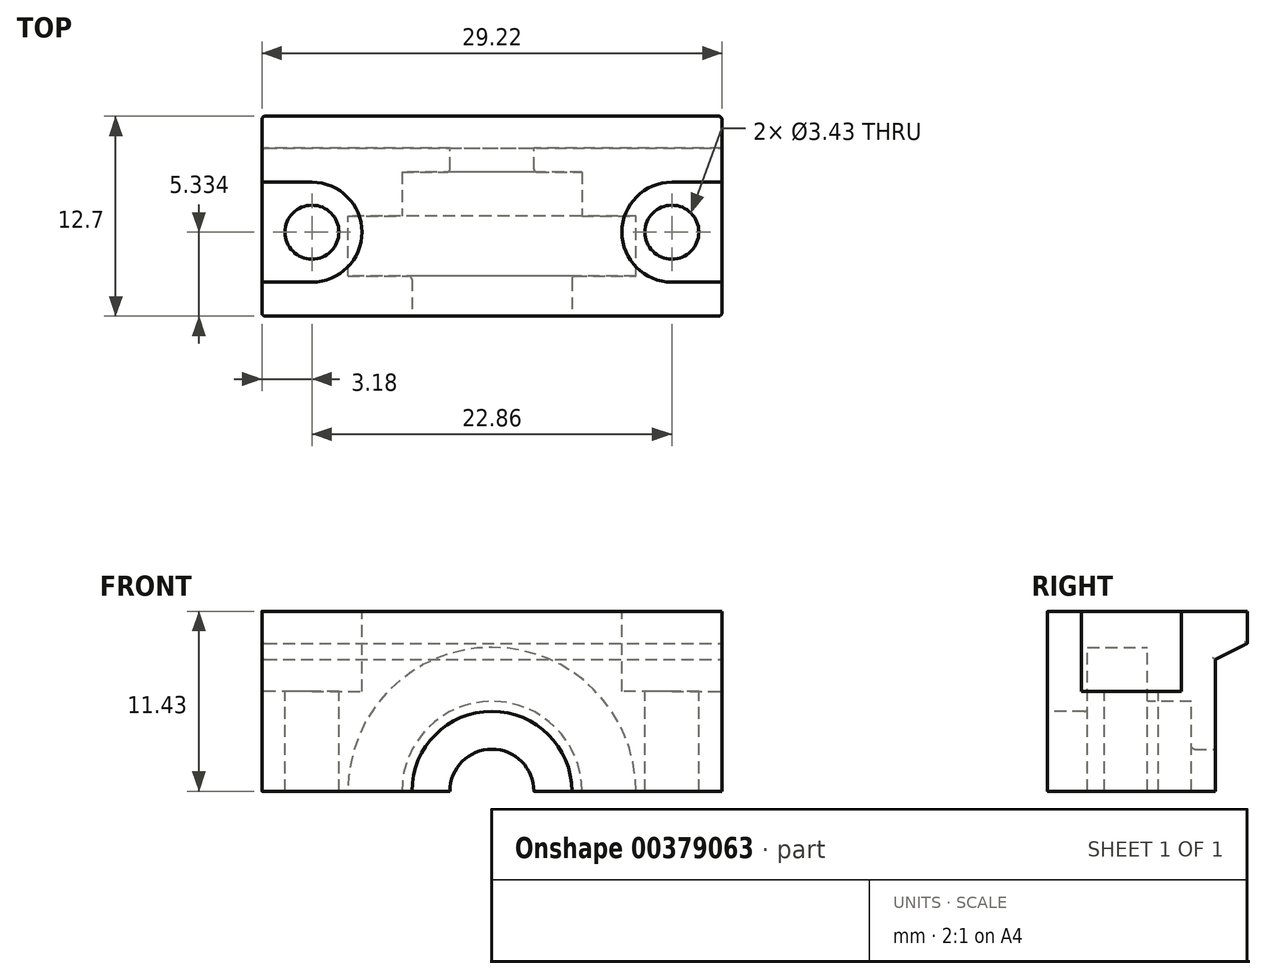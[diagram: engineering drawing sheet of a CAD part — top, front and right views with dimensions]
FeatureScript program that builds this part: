
annotation { "Feature Type Name" : "Feature", "Feature Type Description" : "" }
export const myFeature = defineFeature(function(context is Context, id is Id, definition is map)
    precondition{}
    {
        {
            var Q0;
            Q0=qCreatedBy(makeId("Front.planeOp"),FACE);
            var sketch = newSketch(context, id + "F0", { "sketchPlane" : qUnion([Q0])});
            skLineSegment(sketch, "E0.bottom", {"start": v(14.6, -3.75) * mm, "end": v(-14.6, -3.75) * mm});
            skLineSegment(sketch, "E0.left", {"start": v(14.6, -3.75) * mm, "end": v(14.6, 3.75) * mm});
            skLineSegment(sketch, "E0.right", {"start": v(-14.6, -3.75) * mm, "end": v(-14.6, 3.75) * mm});
            skPoint(sketch, "E0.middle", {"position": v(0, 0) * mm});
            skArc(sketch, "E1", {"start": v(14.6, 3.75) * mm, "mid": v(0, 18.35) * mm, "end": v(-14.6, 3.75) * mm, "construction": true});
            skPoint(sketch, "E2", {"position": v(0, 18.35) * mm});
            skLineSegment(sketch, "E3", {"start": v(-14.6, 3.75) * mm, "end": v(-14.6, 18.35) * mm});
            skLineSegment(sketch, "E4", {"start": v(-14.6, 18.35) * mm, "end": v(14.6, 18.35) * mm});
            skLineSegment(sketch, "E5", {"start": v(14.6, 18.35) * mm, "end": v(14.6, 3.75) * mm});
            skSolve(sketch);
        }
        {
            var Q0;
            Q0=qSketchRegion(id+"F0",true);
            extrude(context, id + "F1", {"entities" : qUnion([Q0]), "depth" : 12.7 * mm});
        }
        {
            var Q0;
            Q0=qCreatedBy(makeId("Front.planeOp"),FACE);
            cPlane(context, id + "F2", {"entities" : qUnion([Q0]), "cplaneType" : CPlaneType.OFFSET, "offset" : 6.35 * mm, "width" : 152.4 * mm, "height" : 152.4 * mm});
        }
        {
            var Q0;
            Q0=qCreatedBy(id+"F2.planeOp",FACE);
            var sketch = newSketch(context, id + "F3", { "sketchPlane" : qUnion([Q0])});
            skLineSegment(sketch, "E6.bottom", {"start": v(9.14, -3.75) * mm, "end": v(-9.14, -3.75) * mm});
            skLineSegment(sketch, "E6.left", {"start": v(9.14, -3.75) * mm, "end": v(9.14, 6.92) * mm});
            skLineSegment(sketch, "E6.right", {"start": v(-9.14, -3.75) * mm, "end": v(-9.14, 6.92) * mm});
            skLineSegment(sketch, "E7", {"start": v(0, -3.75) * mm, "end": v(0, 19.01) * mm, "construction": true});
            skArc(sketch, "E8", {"start": v(9.14, 6.92) * mm, "mid": v(0, 16.07) * mm, "end": v(-9.14, 6.92) * mm});
            skPoint(sketch, "E9", {"position": v(0, 16.07) * mm});
            skSolve(sketch);
        }
        {
            var Q0;
            Q0=qSketchRegion(id+"F3",true);
            extrude(context, id + "F4", {"entities" : qUnion([Q0]), "operationType" : NewBodyOperationType.REMOVE, "depth" : 3.8 * mm});
        }
        {
            var Q0;
            Q0=makeQuery(id+"F1.opExtrude","CAP_FACE",FACE,{"disambiguationData":[OSD([sQuery(id+"F0.wireOp",EDGE,"E0.bottom"),sQuery(id+"F0.wireOp",EDGE,"E0.left"),sQuery(id+"F0.wireOp",EDGE,"E0.right"),sQuery(id+"F0.wireOp",EDGE,"E1")])],"isStart":false});
            var sketch = newSketch(context, id + "F5", { "sketchPlane" : qUnion([Q0])});
            skArc(sketch, "E10", {"start": v(4.85, 5.4) * mm, "mid": v(0, 12) * mm, "end": v(-4.85, 5.4) * mm});
            skLineSegment(sketch, "E11", {"start": v(4.85, 5.4) * mm, "end": v(-4.85, 5.4) * mm, "construction": true});
            skLineSegment(sketch, "E12", {"start": v(4.85, 5.4) * mm, "end": v(6.35, -3.75) * mm});
            skLineSegment(sketch, "E13", {"start": v(6.35, -3.75) * mm, "end": v(-6.35, -3.75) * mm});
            skLineSegment(sketch, "E14", {"start": v(-6.35, -3.75) * mm, "end": v(-4.85, 5.4) * mm});
            skLineSegment(sketch, "E15", {"start": v(0, -3.75) * mm, "end": v(0, 6.92) * mm, "construction": true});
            skSolve(sketch);
        }
        {
            var Q0;
            Q0=qSketchRegion(id+"F5",true);
            extrude(context, id + "F6", {"entities" : qUnion([Q0]), "operationType" : NewBodyOperationType.REMOVE, "oppositeDirection" : true, "depth" : 8.64 * mm});
        }
        {
            var Q0;
            Q0=makeQuery(id+"F1.opExtrude","SWEPT_FACE",FACE,{"disambiguationData":[OSD([sQuery(id+"F0.wireOp",EDGE,"E0.left")])]});
            var sketch = newSketch(context, id + "F7", { "sketchPlane" : qUnion([Q0])});
            skLineSegment(sketch, "E16", {"start": v(0, -1.71) * mm, "end": v(-2.03, -0.7) * mm});
            skLineSegment(sketch, "E17", {"start": v(-2.03, -0.7) * mm, "end": v(-2.03, 15.3) * mm});
            skLineSegment(sketch, "E18", {"start": v(-2.03, 15.3) * mm, "end": v(0, 16.32) * mm});
            skLineSegment(sketch, "E19", {"start": v(0, 16.32) * mm, "end": v(0, -1.71) * mm});
            skLineSegment(sketch, "E20", {"start": v(-2.03, 7.3) * mm, "end": v(0, 7.3) * mm, "construction": true});
            skPoint(sketch, "E20.startSnap0", {"position": v(0, 7.3) * mm});
            skSolve(sketch);
        }
        {
            var Q0;
            Q0=qSketchRegion(id+"F7",true);
            extrude(context, id + "F8", {"entities" : qUnion([Q0]), "operationType" : NewBodyOperationType.REMOVE, "endBound" : BoundingType.THROUGH_ALL, "oppositeDirection" : true, "depth" : 25.4 * mm});
        }
        {
            var Q0;
            Q0=makeQuery(id+"F8.boolean.opBoolean","COPY",FACE,{"derivedFrom":makeQuery(id+"F8.opExtrude","SWEPT_FACE",FACE,{"disambiguationData":[OSD([sQuery(id+"F7.wireOp",EDGE,"E17")])]})});
            var sketch = newSketch(context, id + "F9", { "sketchPlane" : qUnion([Q0])});
            skCircle(sketch, "E21", {"center": v(0, 6.92) * mm, "radius": 2.67 * mm});
            skSolve(sketch);
        }
        {
            var Q0;
            Q0=qSketchRegion(id+"F9",true);
            var Q1;
            Q1=qCreatedBy(id+"F2.planeOp",FACE);
            extrude(context, id + "F10", {"entities" : qUnion([Q0]), "operationType" : NewBodyOperationType.REMOVE, "endBound" : BoundingType.UP_TO_SURFACE, "oppositeDirection" : true, "endBoundEntityFace" : qUnion([Q1]), "depth" : 25.4 * mm});
        }
        {
            var Q0;
            Q0=makeQuery(id+"F1.opExtrude","SWEPT_FACE",FACE,{"disambiguationData":[OSD([sQuery(id+"F0.wireOp",EDGE,"E4")])]});
            var sketch = newSketch(context, id + "F11", { "sketchPlane" : qUnion([Q0])});
            skLineSegment(sketch, "E22", {"start": v(14.6, -7.37) * mm, "end": v(-14.6, -7.37) * mm, "construction": true});
            skArc(sketch, "E23", {"start": v(11.43, -4.2) * mm, "mid": v(8.25, -7.37) * mm, "end": v(11.43, -10.54) * mm});
            skLineSegment(sketch, "E24", {"start": v(0, -12.7) * mm, "end": v(0, 0) * mm, "construction": true});
            skLineSegment(sketch, "E25", {"start": v(11.43, -4.2) * mm, "end": v(14.6, -4.2) * mm});
            skLineSegment(sketch, "E26", {"start": v(14.6, -4.2) * mm, "end": v(14.6, -10.54) * mm});
            skLineSegment(sketch, "E27", {"start": v(14.6, -10.54) * mm, "end": v(11.43, -10.54) * mm});
            skLineSegment(sketch, "E28", {"start": v(11.43, -4.2) * mm, "end": v(11.43, -10.54) * mm, "construction": true});
            skArc(sketch, "E29.MirrorCS", {"start": v(-11.43, -4.2) * mm, "mid": v(-8.26, -7.37) * mm, "end": v(-11.43, -10.54) * mm});
            skLineSegment(sketch, "E30.MirrorCS", {"start": v(-11.43, -4.2) * mm, "end": v(-14.6, -4.2) * mm});
            skLineSegment(sketch, "E31.MirrorCS", {"start": v(-14.6, -10.54) * mm, "end": v(-11.43, -10.54) * mm});
            skLineSegment(sketch, "E32.MirrorCS", {"start": v(-14.6, -4.2) * mm, "end": v(-14.6, -10.54) * mm});
            skSolve(sketch);
        }
        {
            var Q0;
            Q0 = qSketchRegion(id + "F11", true);
            extrude(context, id + "F12", {"entities" : qUnion([Q0]), "operationType" : NewBodyOperationType.REMOVE, "oppositeDirection" : true, "depth" : 5.08 * mm});
        }
        {
            var Q0;
            Q0=makeQuery(id+"F12.boolean.opBoolean","COPY",FACE,{"derivedFrom":makeQuery(id+"F12.opExtrude","CAP_FACE",FACE,{"disambiguationData":[OSD([sQuery(id+"F11.wireOp",EDGE,"E23")])],"isStart":false})});
            var sketch = newSketch(context, id + "F13", { "sketchPlane" : qUnion([Q0])});
            skCircle(sketch, "E33", {"center": v(11.43, -7.37) * mm, "radius": 1.71 * mm});
            skCircle(sketch, "E34", {"center": v(-11.43, -7.37) * mm, "radius": 1.71 * mm});
            skSolve(sketch);
        }
        {
            var Q0;
            Q0 = qSketchRegion(id + "F13", true);
            extrude(context, id + "F14", {"entities" : qUnion([Q0]), "operationType" : NewBodyOperationType.REMOVE, "oppositeDirection" : true, "depth" : 12.7 * mm});
        }
        {
            var Q0;
            Q0=makeQuery(id+"F4.boolean.opBoolean","COPY",FACE,{"derivedFrom":makeQuery(id+"F4.opExtrude","CAP_FACE",FACE,{"disambiguationData":[OSD([sQuery(id+"F3.wireOp",EDGE,"E6.bottom"),sQuery(id+"F3.wireOp",EDGE,"E6.left"),sQuery(id+"F3.wireOp",EDGE,"E6.right"),sQuery(id+"F3.wireOp",EDGE,"E8")])],"isStart":true})});
            var sketch = newSketch(context, id + "F15", { "sketchPlane" : qUnion([Q0])});
            skCircle(sketch, "E35", {"center": v(0, 6.92) * mm, "radius": 5.72 * mm});
            skSolve(sketch);
        }
        {
            var Q0;
            Q0 = qSketchRegion(id + "F15", true);
            extrude(context, id + "F16", {"entities" : qUnion([Q0]), "operationType" : NewBodyOperationType.REMOVE, "oppositeDirection" : true, "depth" : 2.8 * mm});
        }
        {
            var Q0;
            Q0=makeQuery(id+"F1.opExtrude","SWEPT_FACE",FACE,{"disambiguationData":[OSD([sQuery(id+"F0.wireOp",EDGE,"E0.bottom")])]});
            var sketch = newSketch(context, id + "F17", { "sketchPlane" : qUnion([Q0])});
            skLineSegment(sketch, "E36.bottom", {"start": v(-14.6, 12.7) * mm, "end": v(14.6, 12.7) * mm});
            skLineSegment(sketch, "E36.top", {"start": v(-14.6, 0) * mm, "end": v(14.6, 0) * mm});
            skLineSegment(sketch, "E36.left", {"start": v(-14.6, 12.7) * mm, "end": v(-14.6, 0) * mm});
            skLineSegment(sketch, "E36.right", {"start": v(14.6, 12.7) * mm, "end": v(14.6, 0) * mm});
            skSolve(sketch);
        }
        {
            var Q0;
            Q0 = qSketchRegion(id + "F17", true);
            extrude(context, id + "F18", {"entities" : qUnion([Q0]), "operationType" : NewBodyOperationType.REMOVE, "oppositeDirection" : true, "depth" : 10.67 * mm});
        }
        {
            var Q0;
            Q0=makeQuery(id+"F1.opExtrude","CAP_EDGE",EDGE,{"disambiguationData":[OSD([sQuery(id+"F0.wireOp",EDGE,"E0.left"),sQuery(id+"F0.wireOp",EDGE,"E5")])],"isStart":false});
            var Q1;
            Q1=makeQuery(id+"F8.boolean.opBoolean","COPY",EDGE,{"derivedFrom":makeQuery(id+"F8.opExtrude","CAP_EDGE",EDGE,{"disambiguationData":[OSD([sQuery(id+"F7.wireOp",EDGE,"E17")])],"isStart":true})});
            var Q2;
            Q2=makeQuery(id+"F8.boolean.opBoolean","COPY",EDGE,{"derivedFrom":makeQuery(id+"F8.opExtrude","CAP_EDGE",EDGE,{"disambiguationData":[OSD([sQuery(id+"F7.wireOp",EDGE,"E18")])],"isStart":true})});
            var Q3;
            {var subQ0=sQuery(id+"F0.wireOp",EDGE,"E5");var subQ1=sQuery(id+"F0.wireOp",EDGE,"E4");var subQ2=sQuery(id+"F0.wireOp",EDGE,"E0.left");Q3=makeQuery(id+"F8.boolean.opBoolean","SPLIT",EDGE,{"disambiguationData":[TD([makeQuery(id+"F1.opExtrude","SWEPT_FACE",FACE,{"disambiguationData":[OSD([subQ1])]})])],"derivedFrom":makeQuery(id+"F1.opExtrude","CAP_EDGE",EDGE,{"disambiguationData":[OSD([subQ2,subQ0])],"isStart":true})});}
            var Q4;
            Q4=makeQuery(id+"F12.boolean.opBoolean","COPY",EDGE,{"derivedFrom":makeQuery(id+"F12.opExtrude","SWEPT_EDGE",EDGE,{"disambiguationData":[OSD([sQuery(id+"F0.wireOp",EDGE,"E4"),sQuery(id+"F0.wireOp",EDGE,"E5"),sQuery(id+"F11.wireOp",EDGE,"E26"),sQuery(id+"F11.wireOp",EDGE,"E27")])]})});
            var Q5;
            Q5=makeQuery(id+"F12.boolean.opBoolean","COPY",EDGE,{"derivedFrom":makeQuery(id+"F12.opExtrude","SWEPT_EDGE",EDGE,{"disambiguationData":[OSD([sQuery(id+"F0.wireOp",EDGE,"E4"),sQuery(id+"F0.wireOp",EDGE,"E5"),sQuery(id+"F11.wireOp",EDGE,"E25"),sQuery(id+"F11.wireOp",EDGE,"E26")])]})});
            var Q6;
            Q6=makeQuery(id+"F1.opExtrude","CAP_EDGE",EDGE,{"disambiguationData":[OSD([sQuery(id+"F0.wireOp",EDGE,"E0.right"),sQuery(id+"F0.wireOp",EDGE,"E3")])],"isStart":false});
            var Q7;
            Q7=makeQuery(id+"F12.boolean.opBoolean","COPY",EDGE,{"derivedFrom":makeQuery(id+"F12.opExtrude","SWEPT_EDGE",EDGE,{"disambiguationData":[OSD([sQuery(id+"F0.wireOp",EDGE,"E3"),sQuery(id+"F0.wireOp",EDGE,"E4"),sQuery(id+"F11.wireOp",EDGE,"E31.MirrorCS"),sQuery(id+"F11.wireOp",EDGE,"E32.MirrorCS")])]})});
            var Q8;
            Q8=makeQuery(id+"F12.boolean.opBoolean","COPY",EDGE,{"derivedFrom":makeQuery(id+"F12.opExtrude","SWEPT_EDGE",EDGE,{"disambiguationData":[OSD([sQuery(id+"F0.wireOp",EDGE,"E3"),sQuery(id+"F0.wireOp",EDGE,"E4"),sQuery(id+"F11.wireOp",EDGE,"E30.MirrorCS"),sQuery(id+"F11.wireOp",EDGE,"E32.MirrorCS")])]})});
            var Q9;
            {var subQ0=sQuery(id+"F0.wireOp",EDGE,"E4");var subQ1=sQuery(id+"F0.wireOp",EDGE,"E3");var subQ2=sQuery(id+"F0.wireOp",EDGE,"E0.right");Q9=makeQuery(id+"F8.boolean.opBoolean","SPLIT",EDGE,{"disambiguationData":[TD([makeQuery(id+"F1.opExtrude","SWEPT_FACE",FACE,{"disambiguationData":[OSD([subQ0])]})])],"derivedFrom":makeQuery(id+"F1.opExtrude","CAP_EDGE",EDGE,{"disambiguationData":[OSD([subQ2,subQ1])],"isStart":true})});}
            var Q10;
            Q10=makeQuery(id+"F8.boolean.opBoolean","INTERSECT",EDGE,{"derivedFrom":[makeQuery(id+"F1.opExtrude","SWEPT_FACE",FACE,{"disambiguationData":[OSD([sQuery(id+"F0.wireOp",EDGE,"E0.right"),sQuery(id+"F0.wireOp",EDGE,"E3")])]}),makeQuery(id+"F8.opExtrude","SWEPT_FACE",FACE,{"disambiguationData":[OSD([sQuery(id+"F7.wireOp",EDGE,"E17")])]})]});
            var Q11;
            Q11=makeQuery(id+"F8.boolean.opBoolean","INTERSECT",EDGE,{"derivedFrom":[makeQuery(id+"F1.opExtrude","SWEPT_FACE",FACE,{"disambiguationData":[OSD([sQuery(id+"F0.wireOp",EDGE,"E0.right"),sQuery(id+"F0.wireOp",EDGE,"E3")])]}),makeQuery(id+"F8.opExtrude","SWEPT_FACE",FACE,{"disambiguationData":[OSD([sQuery(id+"F7.wireOp",EDGE,"E18")])]})]});
            var Q12;
            Q12=makeQuery(id+"F6.boolean.opBoolean","COPY",EDGE,{"derivedFrom":makeQuery(id+"F6.opExtrude","CAP_EDGE",EDGE,{"disambiguationData":[OSD([sQuery(id+"F5.wireOp",EDGE,"E10")])],"isStart":true})});
            var Q13;
            Q13=makeQuery(id+"F6.boolean.opBoolean","INTERSECT",EDGE,{"derivedFrom":[makeQuery(id+"F4.boolean.opBoolean","COPY",FACE,{"derivedFrom":makeQuery(id+"F4.opExtrude","CAP_FACE",FACE,{"disambiguationData":[OSD([sQuery(id+"F3.wireOp",EDGE,"E6.bottom"),sQuery(id+"F3.wireOp",EDGE,"E6.left"),sQuery(id+"F3.wireOp",EDGE,"E6.right"),sQuery(id+"F3.wireOp",EDGE,"E8")])],"isStart":false})}),makeQuery(id+"F6.opExtrude","SWEPT_FACE",FACE,{"disambiguationData":[OSD([sQuery(id+"F5.wireOp",EDGE,"E10")])]})]});
            var Q14;
            Q14=makeQuery(id+"F16.boolean.opBoolean","COPY",EDGE,{"derivedFrom":makeQuery(id+"F16.opExtrude","CAP_EDGE",EDGE,{"disambiguationData":[OSD([sQuery(id+"F15.wireOp",EDGE,"E35")])],"isStart":true})});
            var Q15;
            Q15=makeQuery(id+"F16.boolean.opBoolean","INTERSECT",EDGE,{"derivedFrom":[makeQuery(id+"F10.boolean.opBoolean","COPY",FACE,{"derivedFrom":makeQuery(id+"F10.opExtrude","SWEPT_FACE",FACE,{"disambiguationData":[OSD([sQuery(id+"F9.wireOp",EDGE,"E21")])]})}),makeQuery(id+"F16.opExtrude","CAP_FACE",FACE,{"disambiguationData":[OSD([sQuery(id+"F15.wireOp",EDGE,"E35")])],"isStart":false})]});
            var Q16;
            Q16=makeQuery(id+"F10.boolean.opBoolean","COPY",EDGE,{"derivedFrom":makeQuery(id+"F10.opExtrude","CAP_EDGE",EDGE,{"disambiguationData":[OSD([sQuery(id+"F9.wireOp",EDGE,"E21")])],"isStart":true})});
            fillet(context, id + "F19", {"entities" : qUnion([Q0, Q1, Q2, Q3, Q4, Q5, Q6, Q7, Q8, Q9, Q10, Q11, Q12, Q13, Q14, Q15, Q16]), "radius" : .2 * mm, "tangentPropagation" : true, "allowEdgeOverflow" : false});
        }
    });
